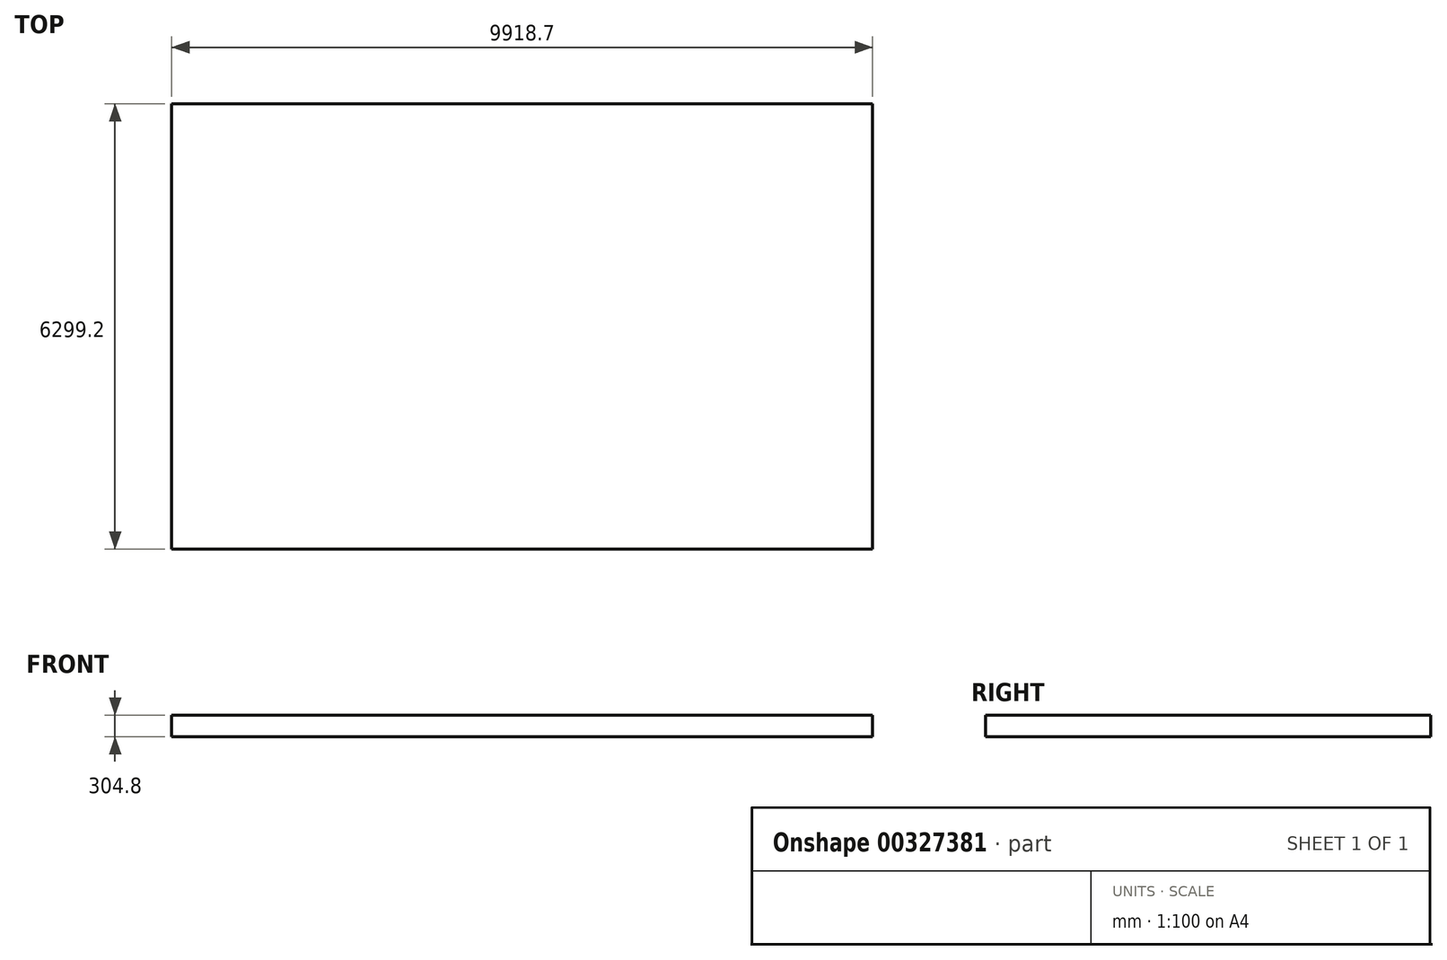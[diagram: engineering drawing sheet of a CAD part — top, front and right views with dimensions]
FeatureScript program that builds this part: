
annotation { "Feature Type Name" : "Feature", "Feature Type Description" : "" }
export const myFeature = defineFeature(function(context is Context, id is Id, definition is map)
    precondition{}
    {
        {
            var Q0;
            Q0=qCreatedBy(makeId("Top.planeOp"),FACE);
            var sketch = newSketch(context, id + "F0", { "sketchPlane" : qUnion([Q0])});
            skLineSegment(sketch, "E0.bottom", {"start": v(0, 0) * mm, "end": v(9918.7, 0) * mm});
            skLineSegment(sketch, "E0.top", {"start": v(0, 6299.2) * mm, "end": v(9918.7, 6299.2) * mm});
            skLineSegment(sketch, "E0.left", {"start": v(0, 0) * mm, "end": v(0, 6299.2) * mm});
            skLineSegment(sketch, "E0.right", {"start": v(9918.7, 0) * mm, "end": v(9918.7, 6299.2) * mm});
            skSolve(sketch);
        }
        {
            var Q0;
            Q0=makeQuery(id+"F0.imprint","IMPRINT",FACE,{"disambiguationData":[TD([[makeQuery(id+"F0.imprint","IMPRINT",EDGE,{"derivedFrom":sQuery(id+"F0.wireOp",EDGE,"E0.bottom")}),1.0]])]});
            extrude(context, id + "F1", {"entities" : qUnion([Q0]), "oppositeDirection" : true, "depth" : 304.8 * mm});
        }
    });
